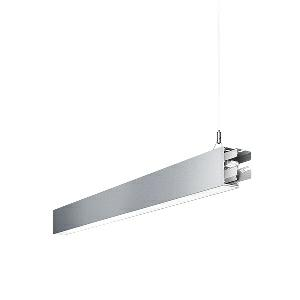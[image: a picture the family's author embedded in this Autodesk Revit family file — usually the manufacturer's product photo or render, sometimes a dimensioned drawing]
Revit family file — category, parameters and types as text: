
# Revit family: dotoo_line_-_dlp_2000_840_d_mid_00805827_a4ea
name_source: partatom
category: Lighting Fixtures
units: mm (PartAtom-declared; Revit-internal decimal feet)

## family parameters
Cut with Voids When Loaded = No
Host = Face
Light Source = No
Part Type = Normal
Room Calculation Point = No
Round Connector Dimension = Use Diameter
Shared = No

## types (1)
- DOTOO.line - DLP 2000/840/D MID (1 x LED, 1700 lm, 4000K)
    Apparent Load = 16 VA
    Approval mark = CE
    CIE Flux Codes = 67 91 98 100 100
    Color Rendering = 80-89
    Color Temperature = 4000K
    Control Gear = Electronic ballast
    Default Elevation = 1800 mm
    Description = DLP 2000/840/D|Suspended luminaire|light source: LED|connected load: 220-240 V, 50/60 Hz|Power consumption: approx. 16 W|standby: approx. 0,15|luminous flux: 1700 lm|luminous efficacy: 106 lm/W|light distribution: Direct|direct ratio: approx. 100 %|colour temperature: Cold white, ca. 4000 K|color rendering index (CRI): >= 80|chromaticity tolerance:  3 SDCM|System of protection: IP 40|technology: Continuously dimmable|luminaire body|material: Sectional aluminium|colour: Silver|lamp cover: Acrylic (PMMA), Clear|mains lead: 1,0 m With free stranded wires|Fastening: Steel cable 0.3 - 0.7 m|glare control: Prism aperture|luminance(L65): <= 3000 cd/m|unified glare rating(4H 8H): <=  19|special features: DALI Load 1x, TouchDIM - dimming via standard switch, Through-wired, up to 18 m on one mains connection, Flicker-free, Suitable as emergency lighting, Mechanical and electrical connection of the individual modules without tools|
    Frequency = 50 Hz
    Height = 110 mm
    Lamp = 1 x LED
    Lamp Light Flux = 1700 lm
    Lamp count = 1
    Length = 1402 mm
    Luminous efficacy = 106 lm/W
    Manufacturer = Waldmann
    ModVariant = No
    Model = 00805827
    Mounting Place = Ceiling
    Mounting Type = Pendant
    Number of Poles = 1
    OnlyDefault = Yes
    Power Factor = 1
    Product Name = DOTOO.line - DLP 2000/840/D MID
    Product group = Suspended luminaire
    ProductGroupID = 9
    Protection Class = Protection class I
    Protection Degree = IP 40
    RLX_Detail_Level = 1
    RLX_Emergency_Light_Flux = 0 lm
    RLX_Emergency_Type = 0
    RLX_Emergency_Type_DB = No
    RlxData = <blob elided: 21965 chars, md5=f907c60c>
    Socket = socket
    Standby Power = 0 W
    System Light Flux = 1700 lm
    System Power = 16 W
    Type Comments = Product without accessories
    Type Image = 113311000-00692597.jpg
    URL = http://relux.com
    VarID = ---
    Voltage = 230 V
    Voltage Range = 220-240 V
    Weight = 0.00 kg
    Width = 60 mm  [stored 0.19685 ft]

note: [stored X ft] marks values corroborated as IEEE doubles in the binary element streams (Revit-internal decimal feet)

## geometry (parser evidence)
native form markers: Blend x4, Sweep x11
no freeform markers — native parametric forms only
